# Revit family: 1441xxx Edward Wall
name_source: partatom
category: Lighting Fixtures
units: mm (PartAtom-declared; Revit-internal decimal feet)

## family parameters
Always vertical = Yes
Cut with Voids When Loaded = No
Host = Wall
Light Source = No
Maintain Annotation Orientation = No
OmniClass Number = 23.80.70.00
OmniClass Title = Lighting
Part Type = Normal
Room Calculation Point = No
Round Connector Dimension = Use Diameter
Shared = No

## types (2) — shared parameters
Apparent Load = 0 VA
Dimmable = Yes
Dimming Method = Lamp Dependent
Driver Included = Not Applicable
Driver Required = No
Lamp = LED
Length of Cable Supplied = Not Applicable
Main Finish = Matt Black
Main Material = Metal - Zinc
Manufacturer = Astro Lighting Ltd
Manufacturer URL - Europe and Rest of World = www.astrolighting.com
Manufacturer URL - North America = us.astrolighting.com
Product Dimensions (MM) = 276 x 110 x 262
Product Location = Indoor
Product Name = Edward Wall
Product Weight (KG) = 0.940
URL = www.astrolighting.com
zero-valued in all types: Default Elevation

## per-type parameters (varying)
| type | ADA compliant | Efficacy (lm/w) | Electrical Class | Light Source Fixed | Location / IP Rating | Power (Watts) | Product SKU |
| CE | Not Applicable | Lamp Dependent (lm/W) | 0 | No | IP20 | Lamp Dependent | 1441001 |
| ETL | Yes - if installed in compliance with ADA §307.2, 308, 309.3, 309.4 | Not Applicable | 1 |  |  |  | 1441007 |

## geometry (parser evidence)
native form markers: Sweep x3
no freeform markers — native parametric forms only
